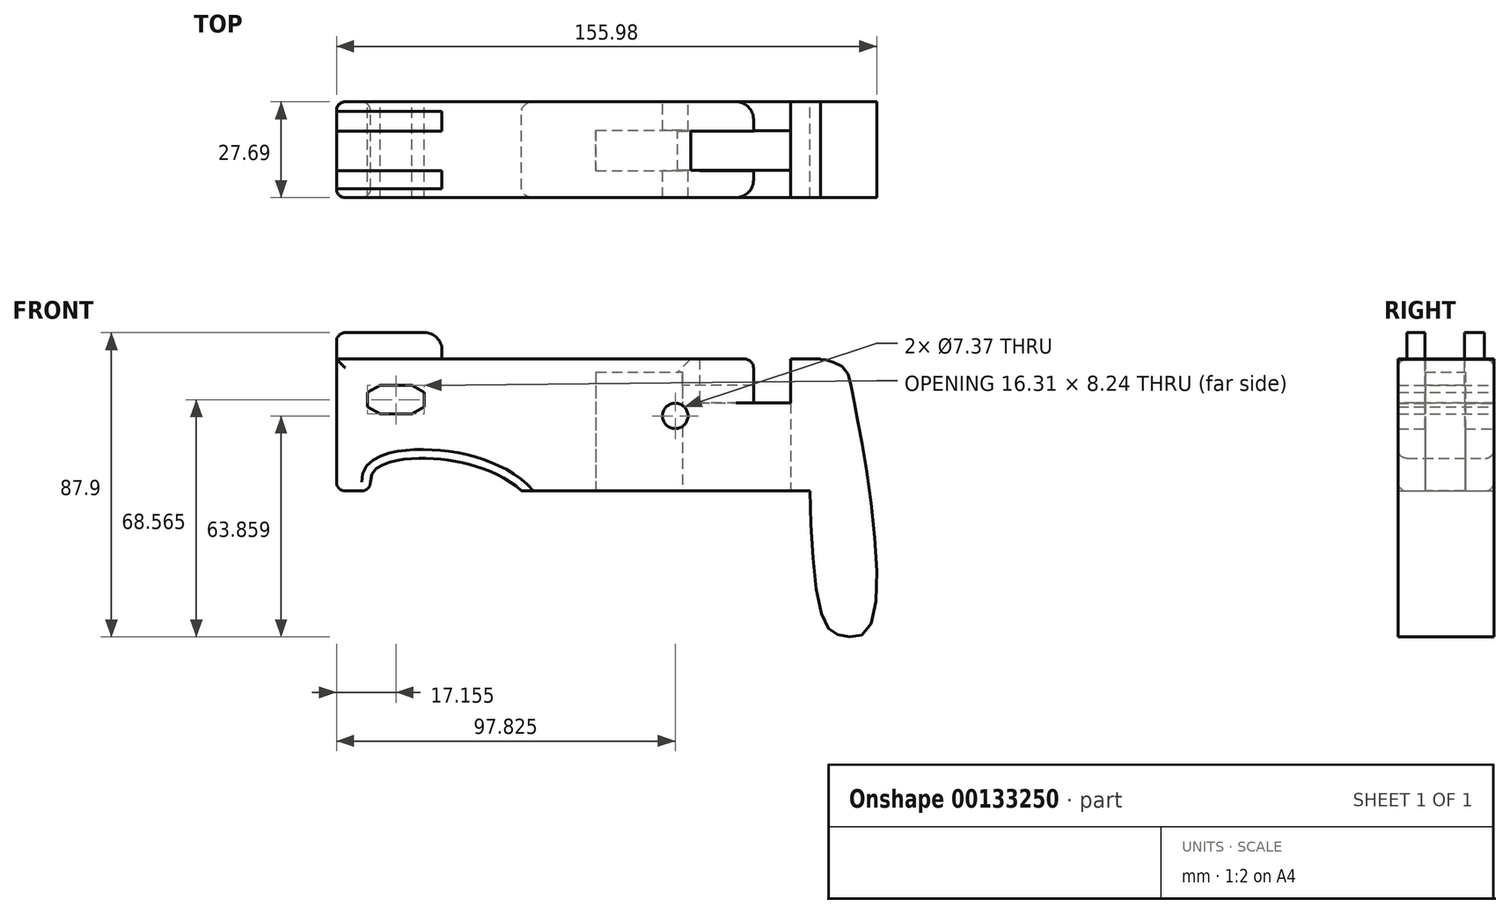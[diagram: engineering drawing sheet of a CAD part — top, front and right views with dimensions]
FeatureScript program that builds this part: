
annotation { "Feature Type Name" : "Feature", "Feature Type Description" : "" }
export const myFeature = defineFeature(function(context is Context, id is Id, definition is map)
    precondition{}
    {
        {
            var Q0;
            Q0=qCreatedBy(makeId("Front.planeOp"),FACE);
            var sketch = newSketch(context, id + "F0", { "sketchPlane" : qUnion([Q0])});
            skLineSegment(sketch, "E0.bottom", {"start": v(-63.42, 38.1) * mm, "end": v(76.28, 38.1) * mm});
            skLineSegment(sketch, "E0.top", {"start": v(-63.42, 0) * mm, "end": v(76.28, 0) * mm});
            skLineSegment(sketch, "E0.left", {"start": v(-63.42, 38.1) * mm, "end": v(-63.42, 0) * mm});
            skLineSegment(sketch, "E0.right", {"start": v(76.28, 38.1) * mm, "end": v(76.28, 0) * mm});
            skLineSegment(sketch, "E1", {"start": v(76.28, 49.39) * mm, "end": v(76.28, 56.48) * mm, "construction": true});
            skLineSegment(sketch, "E2", {"start": v(76.28, -5.47) * mm, "end": v(76.28, -15.92) * mm, "construction": true});
            skSolve(sketch);
        }
        {
            var Q0;
            Q0=qCreatedBy(makeId("Front.planeOp"),FACE);
            var sketch = newSketch(context, id + "F1", { "sketchPlane" : qUnion([Q0])});
            skFitSpline(sketch, "E3", {"points": [v(72.57, 37.14) * mm, v(74.03, 38) * mm, v(75.9, 38) * mm, v(77, 38) * mm, v(79.56, 37.3) * mm, v(83.34, 35.3) * mm, v(85.63, 27.73) * mm, v(90.3, 1.23) * mm, v(89.96, -40.12) * mm, v(82.92, -41.9) * mm, v(77.56, -38.07) * mm, v(73.17, 4.04) * mm, v(72.7, 29.12) * mm, v(72.57, 37.14) * mm]});
            skLineSegment(sketch, "E4", {"start": v(74.78, -25.97) * mm, "end": v(92.56, -25.97) * mm, "construction": true});
            skLineSegment(sketch, "E5", {"start": v(112.88, 37.3) * mm, "end": v(112.88, -36.36) * mm, "construction": true});
            skLineSegment(sketch, "E6", {"start": v(67.24, 0) * mm, "end": v(67.24, -41.9) * mm, "construction": true});
            skLineSegment(sketch, "E7", {"start": v(67.59, 38) * mm, "end": v(71.77, 38) * mm, "construction": true});
            skSolve(sketch);
        }
        {
            var Q0;
            Q0 = qSketchRegion(id + "F0", true);
            extrude(context, id + "F2", {"entities" : qUnion([Q0]), "depth" : 38.1 * mm});
        }
        {
            var Q0;
            Q0 = qSketchRegion(id + "F1", true);
            extrude(context, id + "F3", {"entities" : qUnion([Q0]), "operationType" : NewBodyOperationType.ADD, "depth" : 32.77 * mm});
        }
        {
            var Q0;
            Q0=qCreatedBy(makeId("Top.planeOp"),FACE);
            var sketch = newSketch(context, id + "F4", { "sketchPlane" : qUnion([Q0])});
            skLineSegment(sketch, "E8.bottom", {"start": v(67.66, -13.5) * mm, "end": v(11.4, -13.5) * mm});
            skLineSegment(sketch, "E8.top", {"start": v(67.66, -24.93) * mm, "end": v(11.4, -24.93) * mm});
            skLineSegment(sketch, "E8.left", {"start": v(67.66, -13.5) * mm, "end": v(67.66, -24.93) * mm});
            skLineSegment(sketch, "E8.right", {"start": v(11.4, -13.5) * mm, "end": v(11.4, -24.93) * mm});
            skSolve(sketch);
        }
        {
            var Q0;
            Q0=makeQuery(id+"F2.opExtrude","SWEPT_FACE",FACE,{"disambiguationData":[OSD([sQuery(id+"F0.wireOp",EDGE,"E0.bottom")])]});
            var sketch = newSketch(context, id + "F5", { "sketchPlane" : qUnion([Q0])});
            skLineSegment(sketch, "E9.bottom", {"start": v(56.98, 0) * mm, "end": v(67.68, 0) * mm});
            skLineSegment(sketch, "E9.top", {"start": v(56.98, -38.1) * mm, "end": v(67.68, -38.1) * mm});
            skLineSegment(sketch, "E9.left", {"start": v(56.98, 0) * mm, "end": v(56.98, -38.1) * mm});
            skLineSegment(sketch, "E9.right", {"start": v(67.68, 0) * mm, "end": v(67.68, -38.1) * mm});
            skLineSegment(sketch, "E10", {"start": v(66.5, 1.44) * mm, "end": v(66.5, 12.65) * mm, "construction": true});
            skSolve(sketch);
        }
        {
            var Q0;
            Q0=makeQuery(id+"F5.imprint","IMPRINT",FACE,{"disambiguationData":[TD([[makeQuery(id+"F5.imprint","IMPRINT",EDGE,{"derivedFrom":sQuery(id+"F5.wireOp",EDGE,"E9.bottom")}),-1.0]])]});
            extrude(context, id + "F6", {"entities" : qUnion([Q0]), "operationType" : NewBodyOperationType.REMOVE, "oppositeDirection" : true, "depth" : 12.7 * mm});
        }
        {
            var Q0;
            Q0 = qSketchRegion(id + "F4", true);
            extrude(context, id + "F7", {"entities" : qUnion([Q0]), "operationType" : NewBodyOperationType.REMOVE, "depth" : 30.48 * mm});
        }
        {
            var Q0;
            Q0=qCreatedBy(makeId("Front.planeOp"),FACE);
            var sketch = newSketch(context, id + "F8", { "sketchPlane" : qUnion([Q0])});
            skCircle(sketch, "E11", {"center": v(34.4, 21.68) * mm, "radius": 3.68 * mm});
            skSolve(sketch);
        }
        {
            var Q0;
            Q0 = qSketchRegion(id + "F8", true);
            extrude(context, id + "F9", {"entities" : qUnion([Q0]), "operationType" : NewBodyOperationType.REMOVE, "depth" : 38.1 * mm});
        }
        {
            var Q0;
            {var subQ1=sQuery(id+"F0.wireOp",EDGE,"E0.left");var subQ3=sQuery(id+"F0.wireOp",EDGE,"E0.bottom");Q0=makeQuery(id+"F6.boolean.opBoolean","SPLIT",FACE,{"disambiguationData":[TD([makeQuery(id+"F2.opExtrude","SWEPT_FACE",FACE,{"disambiguationData":[OSD([subQ1])]})])],"derivedFrom":makeQuery(id+"F2.opExtrude","SWEPT_FACE",FACE,{"disambiguationData":[OSD([subQ3])]})});}
            var sketch = newSketch(context, id + "F10", { "sketchPlane" : qUnion([Q0])});
            skLineSegment(sketch, "E12.bottom", {"start": v(56.98, -13.54) * mm, "end": v(41.36, -13.54) * mm});
            skLineSegment(sketch, "E12.top", {"start": v(56.98, -24.97) * mm, "end": v(41.36, -24.97) * mm});
            skLineSegment(sketch, "E12.left", {"start": v(56.98, -13.54) * mm, "end": v(56.98, -24.97) * mm});
            skLineSegment(sketch, "E12.right", {"start": v(41.36, -13.54) * mm, "end": v(41.36, -24.97) * mm});
            skSolve(sketch);
        }
        {
            var Q0;
            Q0 = qSketchRegion(id + "F10", true);
            extrude(context, id + "F11", {"entities" : qUnion([Q0]), "operationType" : NewBodyOperationType.REMOVE, "oppositeDirection" : true, "depth" : 12.7 * mm});
        }
        {
            var Q0;
            Q0=makeQuery(id+"F7.boolean.opBoolean","COPY",EDGE,{"derivedFrom":makeQuery(id+"F7.opExtrude","CAP_EDGE",EDGE,{"disambiguationData":[OSD([sQuery(id+"F4.wireOp",EDGE,"E8.right")])],"isStart":true})});
            var Q1;
            Q1=makeQuery(id+"F11.boolean.opBoolean","INTERSECT",EDGE,{"derivedFrom":[makeQuery(id+"F7.boolean.opBoolean","COPY",FACE,{"derivedFrom":makeQuery(id+"F7.opExtrude","CAP_FACE",FACE,{"disambiguationData":[OSD([sQuery(id+"F4.wireOp",EDGE,"E8.bottom"),sQuery(id+"F4.wireOp",EDGE,"E8.top"),sQuery(id+"F4.wireOp",EDGE,"E8.left"),sQuery(id+"F4.wireOp",EDGE,"E8.right")])],"isStart":false})}),makeQuery(id+"F11.opExtrude","SWEPT_FACE",FACE,{"disambiguationData":[OSD([sQuery(id+"F10.wireOp",EDGE,"E12.right")])]})]});
            chamfer(context, id + "F12", {"entities" : qUnion([Q0, Q1]), "width" : 10.16 * mm, "tangentPropagation" : true});
        }
        {
            var Q0;
            {var subQ1=sQuery(id+"F0.wireOp",EDGE,"E0.left");var subQ3=sQuery(id+"F0.wireOp",EDGE,"E0.bottom");Q0=makeQuery(id+"F6.boolean.opBoolean","SPLIT",FACE,{"disambiguationData":[TD([makeQuery(id+"F2.opExtrude","SWEPT_FACE",FACE,{"disambiguationData":[OSD([subQ1])]})])],"derivedFrom":makeQuery(id+"F2.opExtrude","SWEPT_FACE",FACE,{"disambiguationData":[OSD([subQ3])]})});}
            var sketch = newSketch(context, id + "F13", { "sketchPlane" : qUnion([Q0])});
            skLineSegment(sketch, "E13.bottom", {"start": v(-32.94, -30.2) * mm, "end": v(-63.42, -30.2) * mm});
            skLineSegment(sketch, "E13.top", {"start": v(-32.94, -24.97) * mm, "end": v(-63.42, -24.97) * mm});
            skLineSegment(sketch, "E13.left", {"start": v(-32.94, -24.97) * mm, "end": v(-32.94, -30.2) * mm});
            skLineSegment(sketch, "E13.right", {"start": v(-63.42, -24.97) * mm, "end": v(-63.42, -30.2) * mm});
            skLineSegment(sketch, "E14.bottom", {"start": v(-63.42, -7.83) * mm, "end": v(-32.94, -7.83) * mm});
            skLineSegment(sketch, "E14.top", {"start": v(-63.42, -13.54) * mm, "end": v(-32.94, -13.54) * mm});
            skLineSegment(sketch, "E14.left", {"start": v(-63.42, -7.83) * mm, "end": v(-63.42, -13.54) * mm});
            skLineSegment(sketch, "E14.right", {"start": v(-32.94, -7.83) * mm, "end": v(-32.94, -13.54) * mm});
            skLineSegment(sketch, "E15", {"start": v(-32.94, -13.54) * mm, "end": v(56.98, -13.54) * mm, "construction": true});
            skLineSegment(sketch, "E16", {"start": v(-32.94, -24.97) * mm, "end": v(56.98, -24.97) * mm, "construction": true});
            skLineSegment(sketch, "E17", {"start": v(-32.94, -7.83) * mm, "end": v(56.98, -7.83) * mm, "construction": true});
            skLineSegment(sketch, "E18", {"start": v(-32.94, -30.2) * mm, "end": v(56.98, -30.2) * mm, "construction": true});
            skSolve(sketch);
        }
        {
            var Q0;
            Q0 = qSketchRegion(id + "F13", true);
            extrude(context, id + "F14", {"entities" : qUnion([Q0]), "operationType" : NewBodyOperationType.ADD, "depth" : 7.62 * mm});
        }
        {
            var Q0;
            Q0=qCreatedBy(makeId("Front.planeOp"),FACE);
            var sketch = newSketch(context, id + "F15", { "sketchPlane" : qUnion([Q0])});
            skCircle(sketch, "E19.cCircle", {"center": v(-50.85, 26.39) * mm, "radius": 3.57 * mm, "construction": true});
            skLineSegment(sketch, "E19.0", {"start": v(-50.85, 30.5) * mm, "end": v(-47.28, 28.45) * mm});
            skLineSegment(sketch, "E19.1", {"start": v(-47.28, 28.45) * mm, "end": v(-47.28, 24.32) * mm});
            skLineSegment(sketch, "E19.2", {"start": v(-47.28, 24.32) * mm, "end": v(-50.85, 22.26) * mm});
            skLineSegment(sketch, "E19.3", {"start": v(-50.85, 22.26) * mm, "end": v(-54.42, 24.32) * mm});
            skLineSegment(sketch, "E19.4", {"start": v(-54.42, 24.32) * mm, "end": v(-54.42, 28.45) * mm});
            skLineSegment(sketch, "E19.5", {"start": v(-54.42, 28.45) * mm, "end": v(-50.85, 30.5) * mm});
            skPoint(sketch, "E19.0.midPoint", {"position": v(-49.06, 29.48) * mm});
            skLineSegment(sketch, "E20", {"start": v(-50.85, -11.85) * mm, "end": v(-50.85, -29.91) * mm, "construction": true});
            skCircle(sketch, "E21.cCircle", {"center": v(-41.68, 26.39) * mm, "radius": 3.57 * mm, "construction": true});
            skLineSegment(sketch, "E21.0", {"start": v(-41.68, 22.26) * mm, "end": v(-45.25, 24.32) * mm});
            skLineSegment(sketch, "E21.1", {"start": v(-45.25, 24.32) * mm, "end": v(-45.25, 28.45) * mm});
            skLineSegment(sketch, "E21.2", {"start": v(-45.25, 28.45) * mm, "end": v(-41.68, 30.5) * mm});
            skLineSegment(sketch, "E21.3", {"start": v(-41.68, 30.5) * mm, "end": v(-38.11, 28.45) * mm});
            skLineSegment(sketch, "E21.4", {"start": v(-38.11, 28.45) * mm, "end": v(-38.11, 24.32) * mm});
            skLineSegment(sketch, "E21.5", {"start": v(-38.11, 24.32) * mm, "end": v(-41.68, 22.26) * mm});
            skPoint(sketch, "E21.0.midPoint", {"position": v(-43.46, 23.3) * mm});
            skLineSegment(sketch, "E22", {"start": v(-67.47, 22.26) * mm, "end": v(-67.47, -30.4) * mm, "construction": true});
            skLineSegment(sketch, "E23", {"start": v(-50.85, 30.5) * mm, "end": v(-41.68, 30.5) * mm});
            skLineSegment(sketch, "E24", {"start": v(-41.68, 30.5) * mm, "end": v(-41.68, 22.26) * mm});
            skLineSegment(sketch, "E25", {"start": v(-50.85, 30.5) * mm, "end": v(-50.85, 22.26) * mm});
            skLineSegment(sketch, "E26", {"start": v(-50.85, 22.26) * mm, "end": v(-41.68, 22.26) * mm});
            skLineSegment(sketch, "E27", {"start": v(-45.25, 49.75) * mm, "end": v(56.35, 49.75) * mm, "construction": true});
            skLineSegment(sketch, "E28", {"start": v(-46.96, 30.5) * mm, "end": v(-46.96, 38.13) * mm, "construction": true});
            skSolve(sketch);
        }
        {
            var Q0;
            Q0 = qSketchRegion(id + "F15", true);
            extrude(context, id + "F16", {"entities" : qUnion([Q0]), "operationType" : NewBodyOperationType.REMOVE, "depth" : 38.1 * mm});
        }
        {
            var Q0;
            Q0=makeQuery(id+"F14.opExtrude","CAP_EDGE",EDGE,{"disambiguationData":[OSD([sQuery(id+"F13.wireOp",EDGE,"E14.right")])],"isStart":false});
            var Q1;
            Q1=makeQuery(id+"F14.opExtrude","CAP_EDGE",EDGE,{"disambiguationData":[OSD([sQuery(id+"F13.wireOp",EDGE,"E13.left")])],"isStart":false});
            fillet(context, id + "F17", {"entities" : qUnion([Q0, Q1]), "radius" : 5.08 * mm, "tangentPropagation" : true, "allowEdgeOverflow" : false});
        }
        {
            var Q0;
            Q0=makeQuery(id+"F4.imprint","IMPRINT",FACE,{"disambiguationData":[TD([[makeQuery(id+"F4.imprint","IMPRINT",EDGE,{"derivedFrom":sQuery(id+"F4.wireOp",EDGE,"E8.bottom")}),1.0]])]});
            var sketch = newSketch(context, id + "F18", { "sketchPlane" : qUnion([Q0])});
            skLineSegment(sketch, "E29.bottom", {"start": v(11.5, -25.03) * mm, "end": v(36.41, -25.03) * mm});
            skLineSegment(sketch, "E29.top", {"start": v(11.5, -13.35) * mm, "end": v(36.41, -13.35) * mm});
            skLineSegment(sketch, "E29.left", {"start": v(11.5, -25.03) * mm, "end": v(11.5, -13.35) * mm});
            skLineSegment(sketch, "E29.right", {"start": v(36.41, -25.03) * mm, "end": v(36.41, -13.35) * mm});
            skSolve(sketch);
        }
        {
            var Q0;
            Q0 = qSketchRegion(id + "F18", true);
            extrude(context, id + "F19", {"entities" : qUnion([Q0]), "operationType" : NewBodyOperationType.REMOVE, "depth" : 34.3 * mm});
        }
        {
            var Q0;
            Q0=qCreatedBy(makeId("Front.planeOp"),FACE);
            var sketch = newSketch(context, id + "F20", { "sketchPlane" : qUnion([Q0])});
            skFitSpline(sketch, "E30", {"points": [v(-52.95, 5.35) * mm, v(-30.27, 8.77) * mm, v(-9.95, 0) * mm, v(-8.45, -5.35) * mm, v(-46.08, -5.42) * mm, v(-52.95, 5.35) * mm]});
            skLineSegment(sketch, "E31", {"start": v(-59.34, -43.18) * mm, "end": v(90.52, -43.18) * mm, "construction": true});
            skLineSegment(sketch, "E32", {"start": v(-58.41, 30.15) * mm, "end": v(-54.1, 30.15) * mm});
            skSolve(sketch);
        }
        {
            var Q0;
            Q0 = qSketchRegion(id + "F20", true);
            extrude(context, id + "F21", {"entities" : qUnion([Q0]), "operationType" : NewBodyOperationType.REMOVE, "depth" : 38.1 * mm});
        }
        {
            var Q0;
            Q0=qCreatedBy(makeId("Top.planeOp"),FACE);
            var sketch = newSketch(context, id + "F22", { "sketchPlane" : qUnion([Q0])});
            skLineSegment(sketch, "E33.bottom", {"start": v(-68.34, -5.08) * mm, "end": v(96.76, -5.08) * mm});
            skLineSegment(sketch, "E33.top", {"start": v(-68.34, 0) * mm, "end": v(96.76, 0) * mm});
            skLineSegment(sketch, "E33.left", {"start": v(-68.34, -5.08) * mm, "end": v(-68.34, 0) * mm});
            skLineSegment(sketch, "E33.right", {"start": v(96.76, -5.08) * mm, "end": v(96.76, 0) * mm});
            skLineSegment(sketch, "E34.bottom", {"start": v(-68.34, -32.77) * mm, "end": v(96.76, -32.77) * mm});
            skLineSegment(sketch, "E34.top", {"start": v(-68.34, -38.1) * mm, "end": v(96.76, -38.1) * mm});
            skLineSegment(sketch, "E34.left", {"start": v(-68.34, -32.77) * mm, "end": v(-68.34, -38.1) * mm});
            skLineSegment(sketch, "E34.right", {"start": v(96.76, -32.77) * mm, "end": v(96.76, -38.1) * mm});
            skLineSegment(sketch, "E35", {"start": v(-58.4, -32.77) * mm, "end": v(-58.4, -30.23) * mm, "construction": true});
            skLineSegment(sketch, "E36", {"start": v(-58.42, -5.08) * mm, "end": v(-58.42, -7.62) * mm, "construction": true});
            skLineSegment(sketch, "E37", {"start": v(-58.42, -7.62) * mm, "end": v(-58.4, -30.23) * mm, "construction": true});
            skSolve(sketch);
        }
        {
            var Q0;
            Q0 = qSketchRegion(id + "F22", true);
            extrude(context, id + "F23", {"entities" : qUnion([Q0]), "operationType" : NewBodyOperationType.REMOVE, "depth" : 39.37 * mm});
        }
        {
            var Q0;
            {var subQ0=sQuery(id+"F10.wireOp",EDGE,"E12.top");var subQ1=sQuery(id+"F5.wireOp",EDGE,"E9.left");Q0=makeQuery(id+"F23.boolean.opBoolean","INTERSECT",EDGE,{"derivedFrom":[makeQuery(id+"F11.boolean.opBoolean","SPLIT",FACE,{"disambiguationData":[TD([makeQuery(id+"F11.opExtrude","SWEPT_FACE",FACE,{"disambiguationData":[OSD([subQ0])]})])],"derivedFrom":makeQuery(id+"F6.boolean.opBoolean","COPY",FACE,{"derivedFrom":makeQuery(id+"F6.opExtrude","SWEPT_FACE",FACE,{"disambiguationData":[OSD([subQ1])]})})}),makeQuery(id+"F23.opExtrude","SWEPT_FACE",FACE,{"disambiguationData":[OSD([sQuery(id+"F22.wireOp",EDGE,"E34.bottom")])]})]});}
            var Q1;
            {var subQ0=sQuery(id+"F5.wireOp",EDGE,"E9.left");Q1=makeQuery(id+"F23.boolean.opBoolean","INTERSECT",EDGE,{"derivedFrom":[makeQuery(id+"F11.boolean.opBoolean","SPLIT",FACE,{"disambiguationData":[TD([makeQuery(id+"F3.opExtrude","CAP_FACE",FACE,{"disambiguationData":[OSD([sQuery(id+"F1.wireOp",EDGE,"E3")])],"isStart":true})])],"derivedFrom":makeQuery(id+"F6.boolean.opBoolean","COPY",FACE,{"derivedFrom":makeQuery(id+"F6.opExtrude","SWEPT_FACE",FACE,{"disambiguationData":[OSD([subQ0])]})})}),makeQuery(id+"F23.opExtrude","SWEPT_FACE",FACE,{"disambiguationData":[OSD([sQuery(id+"F22.wireOp",EDGE,"E33.bottom")])]})]});}
            fillet(context, id + "F24", {"entities" : qUnion([Q0, Q1]), "radius" : 5.08 * mm, "tangentPropagation" : true, "allowEdgeOverflow" : false});
        }
        {
            var Q0;
            Q0=makeQuery(id+"F2.opExtrude","SWEPT_EDGE",EDGE,{"disambiguationData":[OSD([sQuery(id+"F0.wireOp",EDGE,"E0.top"),sQuery(id+"F0.wireOp",EDGE,"E0.left")])]});
            var Q1;
            Q1=makeQuery(id+"F14.opExtrude","CAP_EDGE",EDGE,{"disambiguationData":[OSD([sQuery(id+"F13.wireOp",EDGE,"E13.right")])],"isStart":false});
            var Q2;
            Q2=makeQuery(id+"F14.opExtrude","CAP_EDGE",EDGE,{"disambiguationData":[OSD([sQuery(id+"F13.wireOp",EDGE,"E14.left")])],"isStart":false});
            var Q3;
            {var subQ0=sQuery(id+"F0.wireOp",EDGE,"E0.bottom");var subQ1=sQuery(id+"F0.wireOp",EDGE,"E0.left");Q3=makeQuery(id+"F6.boolean.opBoolean","SPLIT",EDGE,{"disambiguationData":[TD([makeQuery(id+"F2.opExtrude","SWEPT_FACE",FACE,{"disambiguationData":[OSD([subQ1])]})])],"derivedFrom":makeQuery(id+"F2.opExtrude","CAP_EDGE",EDGE,{"disambiguationData":[OSD([subQ0])],"isStart":false})});}
            var Q4;
            {var subQ0=sQuery(id+"F0.wireOp",EDGE,"E0.bottom");var subQ1=sQuery(id+"F0.wireOp",EDGE,"E0.left");Q4=makeQuery(id+"F6.boolean.opBoolean","SPLIT",EDGE,{"disambiguationData":[TD([makeQuery(id+"F2.opExtrude","SWEPT_FACE",FACE,{"disambiguationData":[OSD([subQ1])]})])],"derivedFrom":makeQuery(id+"F2.opExtrude","CAP_EDGE",EDGE,{"disambiguationData":[OSD([subQ0])],"isStart":true})});}
            var Q5;
            Q5=makeQuery(id+"F21.boolean.opBoolean","COPY",EDGE,{"derivedFrom":makeQuery(id+"F21.opExtrude","CAP_EDGE",EDGE,{"disambiguationData":[OSD([sQuery(id+"F20.wireOp",EDGE,"E30")])],"isStart":false})});
            var Q6;
            Q6=makeQuery(id+"F21.boolean.opBoolean","COPY",EDGE,{"derivedFrom":makeQuery(id+"F21.opExtrude","CAP_EDGE",EDGE,{"disambiguationData":[OSD([sQuery(id+"F20.wireOp",EDGE,"E30")])],"isStart":true})});
            var Q7;
            Q7=makeQuery(id+"F21.boolean.opBoolean","INTERSECT",EDGE,{"disambiguationData":[OD(0.0)],"derivedFrom":[makeQuery(id+"F2.opExtrude","SWEPT_FACE",FACE,{"disambiguationData":[OSD([sQuery(id+"F0.wireOp",EDGE,"E0.top")])]}),makeQuery(id+"F21.opExtrude","SWEPT_FACE",FACE,{"disambiguationData":[OSD([sQuery(id+"F20.wireOp",EDGE,"E30")])]})]});
            fillet(context, id + "F25", {"entities" : qUnion([Q0, Q1, Q2, Q3, Q4, Q5, Q6, Q7]), "radius" : 2.54 * mm, "tangentPropagation" : true, "allowEdgeOverflow" : false});
        }
        {
            var Q0;
            Q0=makeQuery(id+"F23.boolean.opBoolean","INTERSECT",EDGE,{"derivedFrom":[makeQuery(id+"F21.boolean.opBoolean","COPY",FACE,{"derivedFrom":makeQuery(id+"F21.opExtrude","SWEPT_FACE",FACE,{"disambiguationData":[OSD([sQuery(id+"F20.wireOp",EDGE,"E30")])]})}),makeQuery(id+"F23.opExtrude","SWEPT_FACE",FACE,{"disambiguationData":[OSD([sQuery(id+"F22.wireOp",EDGE,"E34.bottom")])]})]});
            var Q1;
            Q1=makeQuery(id+"F23.boolean.opBoolean","INTERSECT",EDGE,{"derivedFrom":[makeQuery(id+"F21.boolean.opBoolean","COPY",FACE,{"derivedFrom":makeQuery(id+"F21.opExtrude","SWEPT_FACE",FACE,{"disambiguationData":[OSD([sQuery(id+"F20.wireOp",EDGE,"E30")])]})}),makeQuery(id+"F23.opExtrude","SWEPT_FACE",FACE,{"disambiguationData":[OSD([sQuery(id+"F22.wireOp",EDGE,"E33.bottom")])]})]});
            var Q2;
            {var subQ0=sQuery(id+"F0.wireOp",EDGE,"E0.left");var subQ3=sQuery(id+"F0.wireOp",EDGE,"E0.bottom");Q2=makeQuery(id+"F23.boolean.opBoolean","INTERSECT",EDGE,{"derivedFrom":[makeQuery(id+"F6.boolean.opBoolean","SPLIT",FACE,{"disambiguationData":[TD([makeQuery(id+"F2.opExtrude","SWEPT_FACE",FACE,{"disambiguationData":[OSD([subQ0])]})])],"derivedFrom":makeQuery(id+"F2.opExtrude","SWEPT_FACE",FACE,{"disambiguationData":[OSD([subQ3])]})}),makeQuery(id+"F23.opExtrude","SWEPT_FACE",FACE,{"disambiguationData":[OSD([sQuery(id+"F22.wireOp",EDGE,"E34.bottom")])]})]});}
            var Q3;
            {var subQ0=sQuery(id+"F0.wireOp",EDGE,"E0.left");var subQ3=sQuery(id+"F0.wireOp",EDGE,"E0.bottom");Q3=makeQuery(id+"F23.boolean.opBoolean","INTERSECT",EDGE,{"derivedFrom":[makeQuery(id+"F6.boolean.opBoolean","SPLIT",FACE,{"disambiguationData":[TD([makeQuery(id+"F2.opExtrude","SWEPT_FACE",FACE,{"disambiguationData":[OSD([subQ0])]})])],"derivedFrom":makeQuery(id+"F2.opExtrude","SWEPT_FACE",FACE,{"disambiguationData":[OSD([subQ3])]})}),makeQuery(id+"F23.opExtrude","SWEPT_FACE",FACE,{"disambiguationData":[OSD([sQuery(id+"F22.wireOp",EDGE,"E33.bottom")])]})]});}
            fillet(context, id + "F26", {"entities" : qUnion([Q0, Q1, Q2, Q3]), "radius" : 2.54 * mm, "tangentPropagation" : true, "allowEdgeOverflow" : false});
        }
        {
            var Q0;
            Q0=qCreatedBy(makeId("Top.planeOp"),FACE);
            var sketch = newSketch(context, id + "F27", { "sketchPlane" : qUnion([Q0])});
            skLineSegment(sketch, "E38.bottom", {"start": v(92.85, -5.08) * mm, "end": v(72.53, -5.08) * mm});
            skLineSegment(sketch, "E38.top", {"start": v(92.85, 0) * mm, "end": v(72.53, 0) * mm});
            skLineSegment(sketch, "E38.left", {"start": v(92.85, -5.08) * mm, "end": v(92.85, 0) * mm});
            skLineSegment(sketch, "E38.right", {"start": v(72.53, -5.08) * mm, "end": v(72.53, 0) * mm});
            skSolve(sketch);
        }
        {
            var Q0;
            Q0 = qSketchRegion(id + "F27", true);
            extrude(context, id + "F28", {"entities" : qUnion([Q0]), "operationType" : NewBodyOperationType.REMOVE, "oppositeDirection" : true, "depth" : 45.72 * mm});
        }
    });
